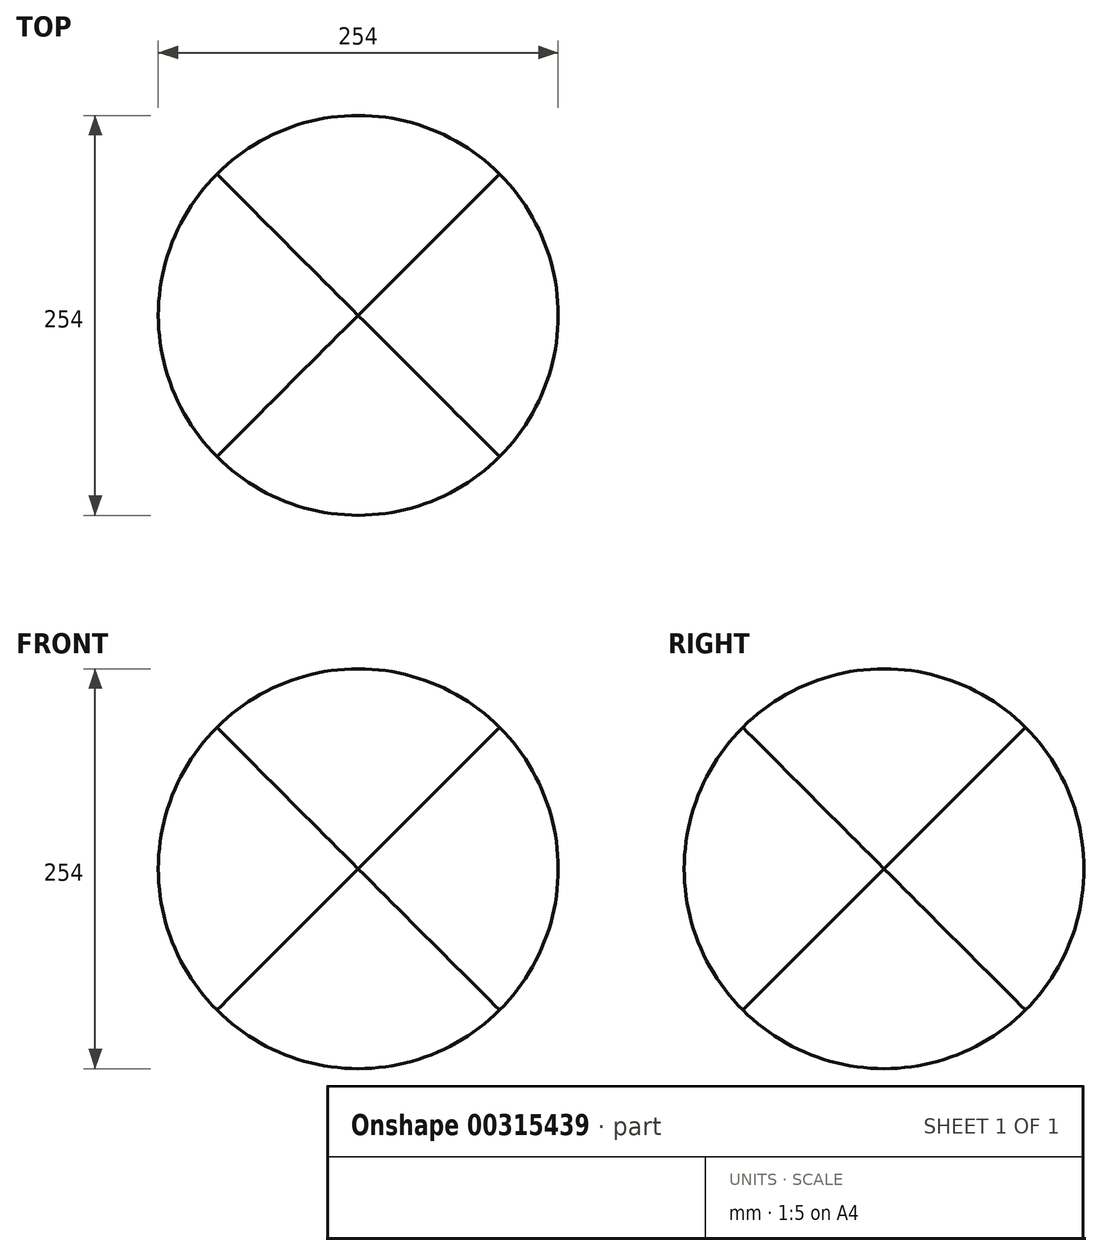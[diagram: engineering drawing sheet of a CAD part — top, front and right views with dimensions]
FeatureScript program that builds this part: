
annotation { "Feature Type Name" : "Feature", "Feature Type Description" : "" }
export const myFeature = defineFeature(function(context is Context, id is Id, definition is map)
    precondition{}
    {
        {
            var Q0;
            Q0=qCreatedBy(makeId("Top.planeOp"),FACE);
            var sketch = newSketch(context, id + "F0", { "sketchPlane" : qUnion([Q0])});
            skCircle(sketch, "E0", {"center": v(0, 0) * mm, "radius": 127 * mm});
            skSolve(sketch);
        }
        {
            var Q0;
            Q0=qCreatedBy(makeId("Front.planeOp"),FACE);
            var sketch = newSketch(context, id + "F1", { "sketchPlane" : qUnion([Q0])});
            skCircle(sketch, "E1", {"center": v(0, 0) * mm, "radius": 127 * mm});
            skSolve(sketch);
        }
        {
            var Q0;
            Q0=qCreatedBy(makeId("Right.planeOp"),FACE);
            var sketch = newSketch(context, id + "F2", { "sketchPlane" : qUnion([Q0])});
            skCircle(sketch, "E2", {"center": v(0, 0) * mm, "radius": 127 * mm});
            skSolve(sketch);
        }
        {
            var Q0;
            Q0=makeQuery(id+"F0.imprint","IMPRINT",FACE,{"disambiguationData":[TD([[makeQuery(id+"F0.imprint","IMPRINT",EDGE,{"derivedFrom":sQuery(id+"F0.wireOp",EDGE,"E0")}),1.0]])]});
            extrude(context, id + "F3", {"entities" : qUnion([Q0]), "endBound" : BoundingType.SYMMETRIC, "depth" : 254 * mm});
        }
        {
            var Q0;
            Q0=makeQuery(id+"F1.imprint","IMPRINT",FACE,{"disambiguationData":[TD([[makeQuery(id+"F1.imprint","IMPRINT",EDGE,{"derivedFrom":sQuery(id+"F1.wireOp",EDGE,"E1")}),1.0]])]});
            extrude(context, id + "F4", {"entities" : qUnion([Q0]), "operationType" : NewBodyOperationType.INTERSECT, "endBound" : BoundingType.SYMMETRIC, "depth" : 254 * mm});
        }
        {
            var Q0;
            Q0=makeQuery(id+"F2.imprint","IMPRINT",FACE,{"disambiguationData":[TD([[makeQuery(id+"F2.imprint","IMPRINT",EDGE,{"derivedFrom":sQuery(id+"F2.wireOp",EDGE,"E2")}),1.0]])]});
            extrude(context, id + "F5", {"entities" : qUnion([Q0]), "operationType" : NewBodyOperationType.INTERSECT, "endBound" : BoundingType.SYMMETRIC, "depth" : 254 * mm});
        }
    });
